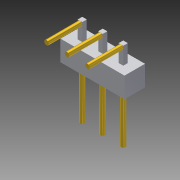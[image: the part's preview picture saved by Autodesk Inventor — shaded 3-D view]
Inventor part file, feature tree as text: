
AUTODESK INVENTOR PART (.ipt)
format: ipt  version: 2011 (Build 150239000, 239)  size: 100,352 bytes
history: native  units: in
note: dims shown in document units (in); Inventor stores cm internally (conversion verified against a paired STEP export)
features: extrude x1, imported_body x1
ambient origin geometry x8: Origin, YZ Plane, XZ Plane, XY Plane, X Axis, Y Axis, Z Axis, Center Point
feature tree (2):
  extrude  "Extrude4"  [1 undecoded]
  imported_body  "Base1"
note: 1 required parameter value undecoded (feature->parameter linkage not recoverable at this tier; creation-order binding heuristic only, values carry confidence <= 0.55)
